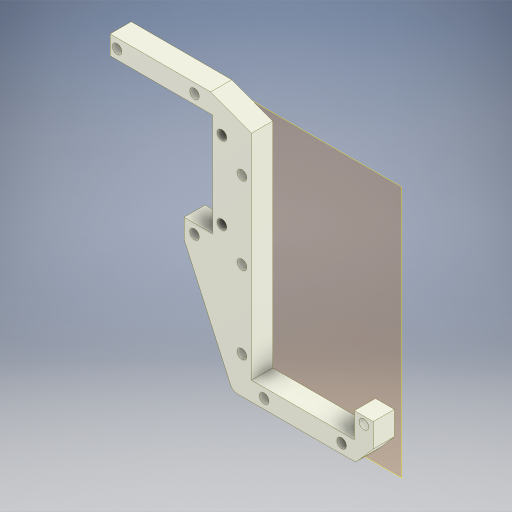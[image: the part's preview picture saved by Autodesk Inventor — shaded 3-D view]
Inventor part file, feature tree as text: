
AUTODESK INVENTOR PART (.ipt)
format: ipt  version: 2024 (Build 280153000, 153)  size: 347,648 bytes
history: native  units: in
note: dims shown in document units (in); Inventor stores cm internally (conversion verified against a paired STEP export)
features: other x5, reference x2, extrude x1, fillet x1, sketch x1
ambient origin geometry x8: Origin, YZ Plane, XZ Plane, XY Plane, X Axis, Y Axis, Z Axis, Center Point
bodies: Body1 (feature_tree)
feature tree (10):
  other  "작업 평면1"
  extrude  "돌출4"  Depth=0.0039in
  fillet  "모깎기3"  Radius=0.0039in
  sketch  "스케치1"
  reference  "참조1"
  reference  "참조2"
  other  "조립품8"
  other  "MX-106T+idle.ipt:3"
  other  "MX-106T:1"
  other  "MX-106T+idle.ipt:2"
